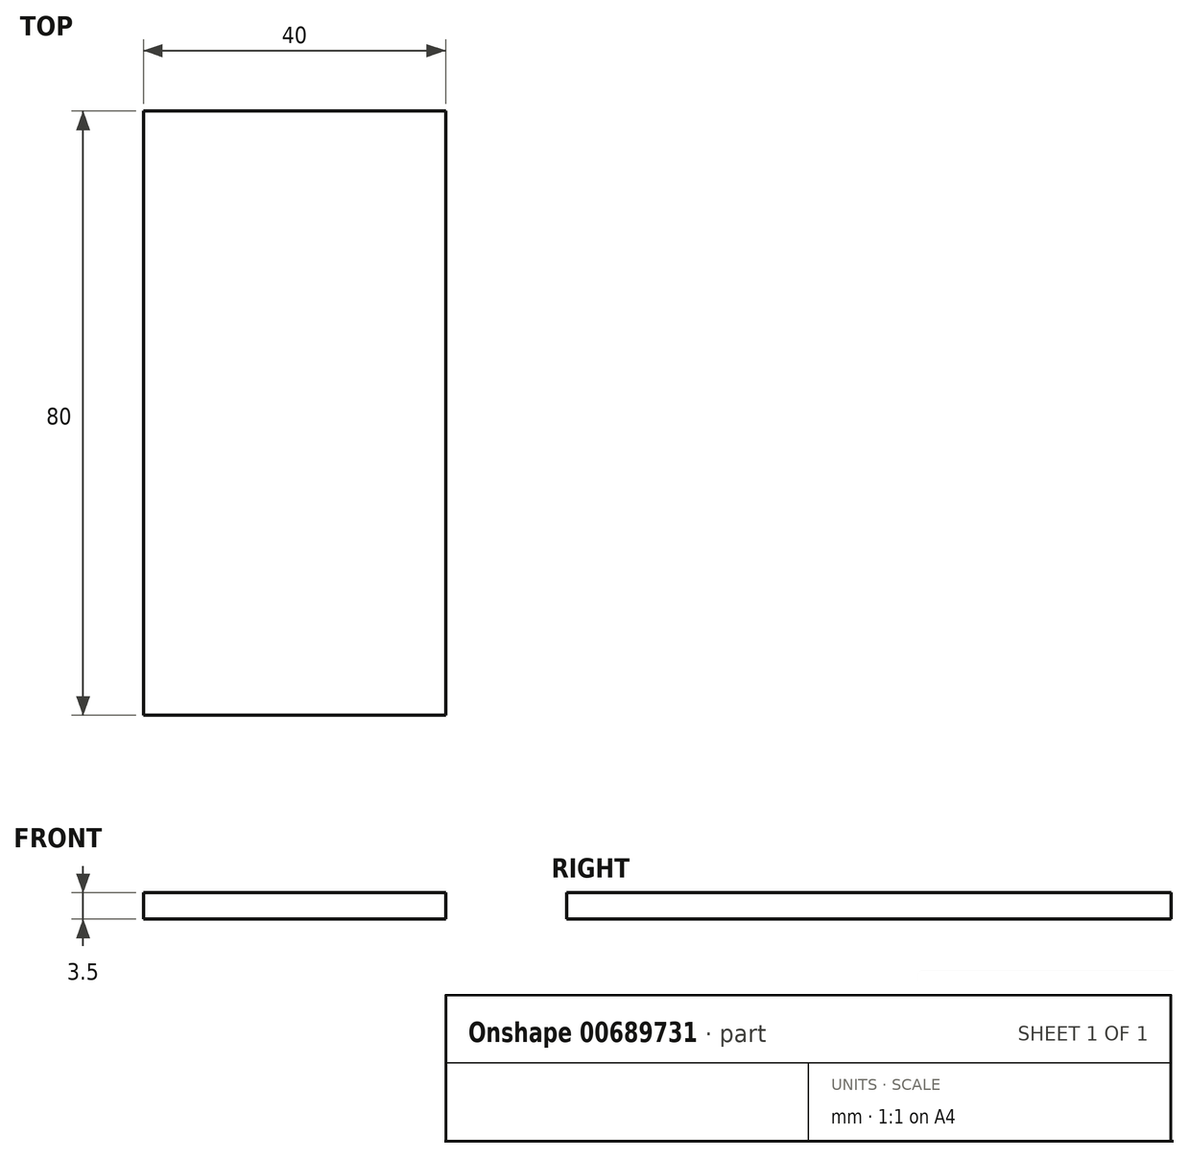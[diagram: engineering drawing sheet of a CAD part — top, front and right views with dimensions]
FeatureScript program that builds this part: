
annotation { "Feature Type Name" : "Feature", "Feature Type Description" : "" }
export const myFeature = defineFeature(function(context is Context, id is Id, definition is map)
    precondition{}
    {
        {
            var Q0;
            Q0=qCreatedBy(makeId("Top.planeOp"),FACE);
            var sketch = newSketch(context, id + "F0", { "sketchPlane" : qUnion([Q0])});
            skLineSegment(sketch, "E0.bottom", {"start": v(20, 40) * mm, "end": v(-20, 40) * mm});
            skLineSegment(sketch, "E0.top", {"start": v(20, -40) * mm, "end": v(-20, -40) * mm});
            skLineSegment(sketch, "E0.left", {"start": v(20, 40) * mm, "end": v(20, -40) * mm});
            skLineSegment(sketch, "E0.right", {"start": v(-20, 40) * mm, "end": v(-20, -40) * mm});
            skPoint(sketch, "E0.middle", {"position": v(0, 0) * mm});
            skLineSegment(sketch, "E1", {"start": v(0, 0) * mm, "end": v(20, 0) * mm});
            skLineSegment(sketch, "E2", {"start": v(20, 0) * mm, "end": v(10, 0) * mm});
            skLineSegment(sketch, "E3", {"start": v(10, 0) * mm, "end": v(15, 0) * mm});
            skLineSegment(sketch, "E4.bottom", {"start": v(17.5, 15) * mm, "end": v(12.5, 15) * mm});
            skLineSegment(sketch, "E4.top", {"start": v(17.5, -15) * mm, "end": v(12.5, -15) * mm});
            skLineSegment(sketch, "E4.left", {"start": v(17.5, 15) * mm, "end": v(17.5, -15) * mm});
            skLineSegment(sketch, "E4.right", {"start": v(12.5, 15) * mm, "end": v(12.5, -15) * mm});
            skPoint(sketch, "E4.middle", {"position": v(15, 0) * mm});
            skSolve(sketch);
        }
        {
            var Q0;
            {var subQ1=sQuery(id+"F0.wireOp",EDGE,"E4.bottom");Q0=makeQuery(id+"F0.imprint","IMPRINT",FACE,{"disambiguationData":[TD([[makeQuery(id+"F0.imprint","IMPRINT",EDGE,{"derivedFrom":subQ1}),1.0]])]});}
            var Q1;
            {var subQ0=sQuery(id+"F0.wireOp",EDGE,"E4.top");Q1=makeQuery(id+"F0.imprint","IMPRINT",FACE,{"disambiguationData":[TD([[makeQuery(id+"F0.imprint","IMPRINT",EDGE,{"derivedFrom":subQ0}),-1.0]])]});}
            var Q2;
            {var subQ6=sQuery(id+"F0.wireOp",EDGE,"E0.bottom");Q2=makeQuery(id+"F0.imprint","IMPRINT",FACE,{"disambiguationData":[TD([[makeQuery(id+"F0.imprint","IMPRINT",EDGE,{"derivedFrom":subQ6}),1.0]])]});}
            extrude(context, id + "F1", {"entities" : qUnion([Q0, Q1, Q2]), "depth" : 3.5 * mm, "offsetDistance" : 25 * mm});
        }
    });
